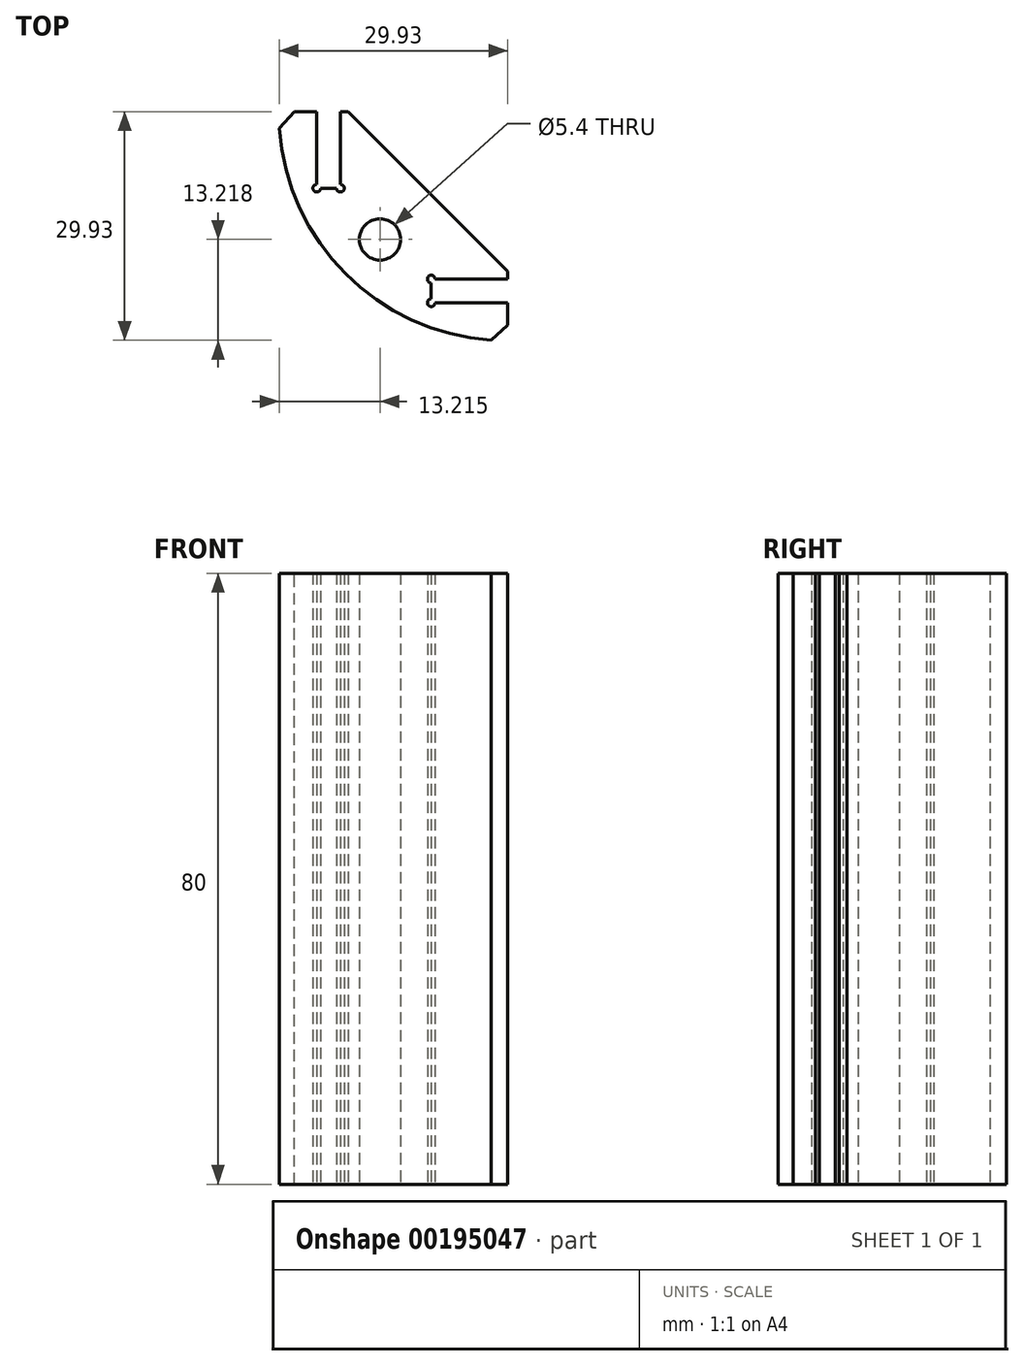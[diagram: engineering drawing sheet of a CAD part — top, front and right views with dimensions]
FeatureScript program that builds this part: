
annotation { "Feature Type Name" : "Feature", "Feature Type Description" : "" }
export const myFeature = defineFeature(function(context is Context, id is Id, definition is map)
    precondition{}
    {
        {
            var Q0;
            Q0=qCreatedBy(makeId("Top.planeOp"),FACE);
            var sketch = newSketch(context, id + "F0", { "sketchPlane" : qUnion([Q0])});
            skPoint(sketch, "E0.middle", {"position": v(0, 0) * mm});
            skCircle(sketch, "E1", {"center": v(-81, -61) * mm, "radius": 1.5 * mm});
            skCircle(sketch, "E2", {"center": v(-81, 61) * mm, "radius": 1.5 * mm});
            skPoint(sketch, "E3.visualSharp", {"position": v(-125, -90) * mm});
            skArc(sketch, "E3.filletArc", {"start": v(-135.97, -74.12) * mm, "mid": v(-127.19, -95.33) * mm, "end": v(-105.97, -104.12) * mm});
            skLineSegment(sketch, "E4", {"start": v(-105.97, -74.12) * mm, "end": v(-127.19, -95.33) * mm, "construction": true});
            skLineSegment(sketch, "E5", {"start": v(-135.97, -74.12) * mm, "end": v(-105.97, -74.12) * mm});
            skLineSegment(sketch, "E6", {"start": v(-105.97, -104.12) * mm, "end": v(-105.97, -74.12) * mm});
            skLineSegment(sketch, "E7.bottom", {"start": v(-127.87, -84.12) * mm, "end": v(-130.97, -84.12) * mm});
            skLineSegment(sketch, "E7.top", {"start": v(-127.87, -64.12) * mm, "end": v(-130.97, -64.12) * mm});
            skLineSegment(sketch, "E7.left", {"start": v(-127.87, -84.12) * mm, "end": v(-127.87, -64.12) * mm});
            skLineSegment(sketch, "E7.right", {"start": v(-130.97, -84.12) * mm, "end": v(-130.97, -64.12) * mm});
            skPoint(sketch, "E7.middle", {"position": v(-129.42, -74.12) * mm});
            skLineSegment(sketch, "E8.bottom", {"start": v(-95.97, -99.12) * mm, "end": v(-115.97, -99.12) * mm});
            skLineSegment(sketch, "E8.top", {"start": v(-95.97, -96.02) * mm, "end": v(-115.97, -96.02) * mm});
            skLineSegment(sketch, "E8.left", {"start": v(-95.97, -99.12) * mm, "end": v(-95.97, -96.02) * mm});
            skLineSegment(sketch, "E8.right", {"start": v(-115.97, -99.12) * mm, "end": v(-115.97, -96.02) * mm});
            skPoint(sketch, "E8.middle", {"position": v(-105.97, -89.12) * mm});
            skCircle(sketch, "E9", {"center": v(-122.68, -90.83) * mm, "radius": 2.7 * mm});
            skLineSegment(sketch, "E10", {"start": v(-146.47, -4.12) * mm, "end": v(-133.93, -4.12) * mm, "construction": true});
            skLineSegment(sketch, "E11", {"start": v(-26.47, -104.12) * mm, "end": v(-26.47, -81.3) * mm, "construction": true});
            skLineSegment(sketch, "E12.MirrorCS", {"start": v(74.93, -84.12) * mm, "end": v(78.03, -84.12) * mm});
            skLineSegment(sketch, "E13.MirrorCS", {"start": v(63.03, -99.12) * mm, "end": v(63.03, -96.02) * mm});
            skLineSegment(sketch, "E14.MirrorCS", {"start": v(43.03, -96.02) * mm, "end": v(63.03, -96.02) * mm});
            skLineSegment(sketch, "E15.MirrorCS", {"start": v(74.93, -84.12) * mm, "end": v(74.93, -64.12) * mm});
            skLineSegment(sketch, "E16.MirrorCS", {"start": v(74.93, -64.12) * mm, "end": v(78.03, -64.12) * mm});
            skLineSegment(sketch, "E17.MirrorCS", {"start": v(43.03, -99.12) * mm, "end": v(63.03, -99.12) * mm});
            skLineSegment(sketch, "E18.MirrorCS", {"start": v(78.03, -84.12) * mm, "end": v(78.03, -64.12) * mm});
            skCircle(sketch, "E19.MirrorC", {"center": v(69.74, -90.83) * mm, "radius": 2.7 * mm});
            skLineSegment(sketch, "E20.MirrorCS", {"start": v(43.03, -99.12) * mm, "end": v(43.03, -96.02) * mm});
            skLineSegment(sketch, "E21.MirrorCS", {"start": v(83.03, -74.12) * mm, "end": v(53.03, -74.12) * mm});
            skArc(sketch, "E22.MirrorCS", {"start": v(53.03, -98.02) * mm, "mid": v(58.28, -79.38) * mm, "end": v(76.93, -74.12) * mm});
            skPoint(sketch, "E23.MirrorP", {"position": v(76.48, -74.12) * mm});
            skLineSegment(sketch, "E24.MirrorCS", {"start": v(53.03, -74.12) * mm, "end": v(74.24, -95.33) * mm, "construction": true});
            skPoint(sketch, "E25.MirrorP", {"position": v(53.03, -89.12) * mm});
            skLineSegment(sketch, "E26.MirrorCS", {"start": v(53.03, -104.12) * mm, "end": v(53.03, -74.12) * mm});
            skArc(sketch, "E27.MirrorCS", {"start": v(83.03, -74.12) * mm, "mid": v(74.24, -95.33) * mm, "end": v(53.03, -104.12) * mm});
            skPoint(sketch, "E28.MirrorP", {"position": v(72.05, -90) * mm});
            skLineSegment(sketch, "E29.MirrorCS", {"start": v(-127.87, 75.88) * mm, "end": v(-130.97, 75.88) * mm});
            skLineSegment(sketch, "E30.MirrorCS", {"start": v(-115.97, 90.88) * mm, "end": v(-115.97, 87.78) * mm});
            skLineSegment(sketch, "E31.MirrorCS", {"start": v(-95.97, 87.78) * mm, "end": v(-115.97, 87.78) * mm});
            skLineSegment(sketch, "E32.MirrorCS", {"start": v(-127.87, 75.88) * mm, "end": v(-127.87, 55.88) * mm});
            skLineSegment(sketch, "E33.MirrorCS", {"start": v(-127.87, 55.88) * mm, "end": v(-130.97, 55.88) * mm});
            skLineSegment(sketch, "E34.MirrorCS", {"start": v(-95.97, 90.88) * mm, "end": v(-115.97, 90.88) * mm});
            skLineSegment(sketch, "E35.MirrorCS", {"start": v(-95.97, 90.88) * mm, "end": v(-95.97, 87.78) * mm});
            skLineSegment(sketch, "E36.MirrorCS", {"start": v(-130.97, 75.88) * mm, "end": v(-130.97, 55.88) * mm});
            skCircle(sketch, "E37.MirrorC", {"center": v(-122.68, 82.59) * mm, "radius": 2.7 * mm});
            skLineSegment(sketch, "E38.MirrorCS", {"start": v(-135.97, 65.88) * mm, "end": v(-105.97, 65.88) * mm});
            skPoint(sketch, "E39.MirrorP", {"position": v(-129.42, 65.88) * mm});
            skPoint(sketch, "E40.MirrorP", {"position": v(-105.97, 80.88) * mm});
            skLineSegment(sketch, "E41.MirrorCS", {"start": v(-105.97, 65.88) * mm, "end": v(-127.19, 87.1) * mm, "construction": true});
            skPoint(sketch, "E42.MirrorP", {"position": v(-125, 81.76) * mm});
            skLineSegment(sketch, "E43.MirrorCS", {"start": v(-105.97, 95.88) * mm, "end": v(-105.97, 65.88) * mm});
            skArc(sketch, "E44.MirrorCS", {"start": v(-105.97, 89.78) * mm, "mid": v(-111.23, 71.13) * mm, "end": v(-129.87, 65.88) * mm});
            skArc(sketch, "E45.MirrorCS", {"start": v(-135.97, 65.88) * mm, "mid": v(-127.19, 87.1) * mm, "end": v(-105.97, 95.88) * mm});
            skLineSegment(sketch, "E46.MirrorCS", {"start": v(78.03, 75.88) * mm, "end": v(78.03, 55.88) * mm});
            skCircle(sketch, "E47.MirrorC", {"center": v(69.74, 82.59) * mm, "radius": 2.7 * mm});
            skLineSegment(sketch, "E48.MirrorCS", {"start": v(74.93, 55.88) * mm, "end": v(78.03, 55.88) * mm});
            skLineSegment(sketch, "E49.MirrorCS", {"start": v(43.03, 90.88) * mm, "end": v(63.03, 90.88) * mm});
            skLineSegment(sketch, "E50.MirrorCS", {"start": v(74.93, 75.88) * mm, "end": v(78.03, 75.88) * mm});
            skLineSegment(sketch, "E51.MirrorCS", {"start": v(43.03, 87.78) * mm, "end": v(63.03, 87.78) * mm});
            skLineSegment(sketch, "E52.MirrorCS", {"start": v(74.93, 75.88) * mm, "end": v(74.93, 55.88) * mm});
            skLineSegment(sketch, "E53.MirrorCS", {"start": v(43.03, 90.88) * mm, "end": v(43.03, 87.78) * mm});
            skLineSegment(sketch, "E54.MirrorCS", {"start": v(63.03, 90.88) * mm, "end": v(63.03, 87.78) * mm});
            skPoint(sketch, "E55.MirrorP", {"position": v(53.03, 80.88) * mm});
            skArc(sketch, "E56.MirrorCS", {"start": v(83.03, 65.88) * mm, "mid": v(74.24, 87.1) * mm, "end": v(53.03, 95.88) * mm});
            skPoint(sketch, "E57.MirrorP", {"position": v(76.48, 65.88) * mm});
            skLineSegment(sketch, "E58.MirrorCS", {"start": v(53.03, 65.88) * mm, "end": v(74.24, 87.1) * mm, "construction": true});
            skLineSegment(sketch, "E59.MirrorCS", {"start": v(83.03, 65.88) * mm, "end": v(53.03, 65.88) * mm});
            skArc(sketch, "E60.MirrorCS", {"start": v(53.03, 89.78) * mm, "mid": v(58.28, 71.13) * mm, "end": v(76.93, 65.88) * mm});
            skPoint(sketch, "E61.MirrorP", {"position": v(72.05, 81.76) * mm});
            skLineSegment(sketch, "E62.MirrorCS", {"start": v(-105.97, 95.88) * mm, "end": v(74.03, 95.88) * mm});
            skLineSegment(sketch, "E63.MirrorCS", {"start": v(53.03, 95.88) * mm, "end": v(53.03, 65.88) * mm});
            skLineSegment(sketch, "E64", {"start": v(83.03, 65.88) * mm, "end": v(83.03, -74.12) * mm});
            skLineSegment(sketch, "E65.bottom", {"start": v(-107.47, 56.88) * mm, "end": v(54.53, 56.88) * mm, "construction": true});
            skLineSegment(sketch, "E65.top", {"start": v(-107.47, -65.12) * mm, "end": v(54.53, -65.12) * mm, "construction": true});
            skLineSegment(sketch, "E65.left", {"start": v(-107.47, 56.88) * mm, "end": v(-107.47, -65.12) * mm, "construction": true});
            skLineSegment(sketch, "E65.right", {"start": v(54.53, 56.88) * mm, "end": v(54.53, -65.12) * mm, "construction": true});
            skPoint(sketch, "E65.middle", {"position": v(-26.47, -4.12) * mm});
            skLineSegment(sketch, "E66.bottom", {"start": v(-127.87, 55.88) * mm, "end": v(-133.02, 55.88) * mm});
            skLineSegment(sketch, "E66.top", {"start": v(-127.92, -64.12) * mm, "end": v(-130.97, -64.12) * mm});
            skLineSegment(sketch, "E67.left", {"start": v(-95.97, -96.02) * mm, "end": v(-95.97, -99.12) * mm});
            skLineSegment(sketch, "E67.right", {"start": v(43.03, -96.02) * mm, "end": v(43.03, -99.12) * mm});
            skPoint(sketch, "E68", {"position": v(-130.97, -74.12) * mm});
            skPoint(sketch, "E69", {"position": v(-105.97, -99.12) * mm});
            skPoint(sketch, "E70", {"position": v(-127.87, -74.12) * mm});
            skPoint(sketch, "E71", {"position": v(-105.97, -96.02) * mm});
            skCircle(sketch, "E72", {"center": v(-130.97, -84.12) * mm, "radius": 0.5 * mm});
            skCircle(sketch, "E73", {"center": v(-127.87, -84.12) * mm, "radius": 0.5 * mm});
            skCircle(sketch, "E74", {"center": v(-115.97, -96.02) * mm, "radius": 0.5 * mm});
            skCircle(sketch, "E75", {"center": v(-115.97, -99.12) * mm, "radius": 0.5 * mm});
            skLineSegment(sketch, "E76", {"start": v(-126.87, -74.12) * mm, "end": v(-105.97, -95.02) * mm});
            skSolve(sketch);
        }
        {
            var Q0;
            Q0=makeQuery(id+"F0.imprint","IMPRINT",FACE,{"disambiguationData":[TD([[makeQuery(id+"F0.imprint","IMPRINT",EDGE,{"derivedFrom":sQuery(id+"F0.wireOp",EDGE,"E3.filletArc")}),1.0]])]});
            extrude(context, id + "F1", {"entities" : qUnion([Q0]), "depth" : 80 * mm});
        }
        {
            var Q0;
            Q0=makeQuery(id+"F1.opExtrude","SWEPT_EDGE",EDGE,{"disambiguationData":[OSD([sQuery(id+"F0.wireOp",EDGE,"E3.filletArc"),sQuery(id+"F0.wireOp",EDGE,"E6")])]});
            var Q1;
            Q1=makeQuery(id+"F1.opExtrude","SWEPT_EDGE",EDGE,{"disambiguationData":[OSD([sQuery(id+"F0.wireOp",EDGE,"E3.filletArc"),sQuery(id+"F0.wireOp",EDGE,"E5")])]});
            chamfer(context, id + "F2", {"entities" : qUnion([Q0, Q1]), "width" : 2 * mm, "tangentPropagation" : true});
        }
    });
